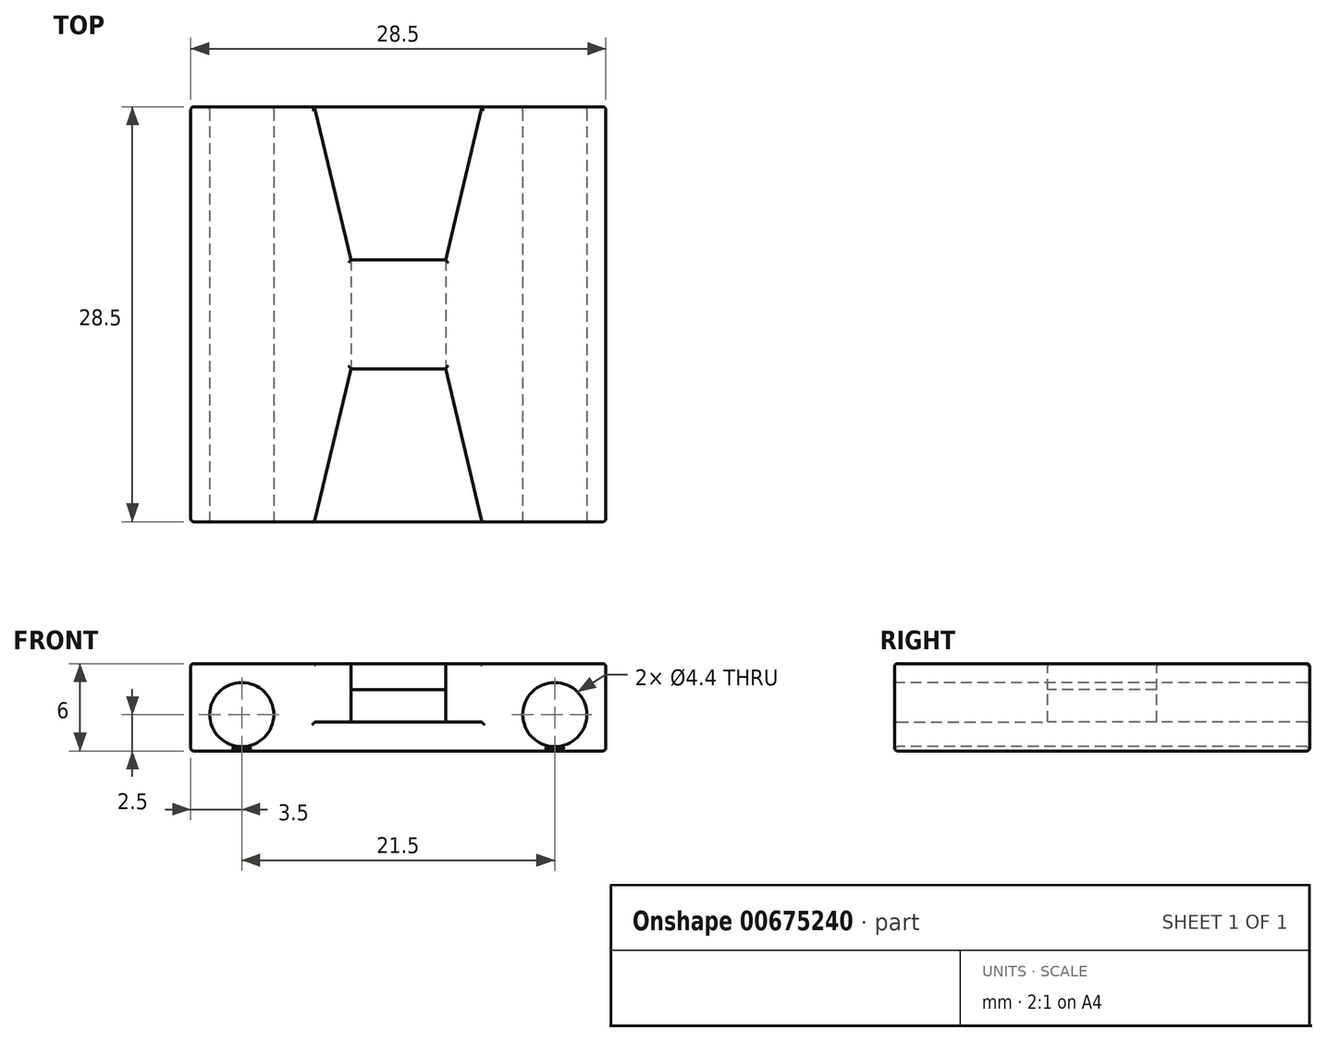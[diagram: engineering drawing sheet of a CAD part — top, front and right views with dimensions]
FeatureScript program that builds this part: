
annotation { "Feature Type Name" : "Feature", "Feature Type Description" : "" }
export const myFeature = defineFeature(function(context is Context, id is Id, definition is map)
    precondition{}
    {
        {
            var Q0;
            Q0=qCreatedBy(makeId("Top.planeOp"),FACE);
            var sketch = newSketch(context, id + "F0", { "sketchPlane" : qUnion([Q0])});
            skLineSegment(sketch, "E0.bottom", {"start": v(14.25, -14.25) * mm, "end": v(-14.25, -14.25) * mm});
            skLineSegment(sketch, "E0.top", {"start": v(14.25, 14.25) * mm, "end": v(-14.25, 14.25) * mm});
            skLineSegment(sketch, "E0.left", {"start": v(14.25, -14.25) * mm, "end": v(14.25, 14.25) * mm});
            skLineSegment(sketch, "E0.right", {"start": v(-14.25, -14.25) * mm, "end": v(-14.25, 14.25) * mm});
            skPoint(sketch, "E0.middle", {"position": v(0, 0) * mm});
            skSolve(sketch);
        }
        {
            var Q0;
            Q0 = qSketchRegion(id + "F0", true);
            extrude(context, id + "F1", {"entities" : qUnion([Q0]), "depth" : 6 * mm, "offsetDistance" : 25 * mm});
        }
        {
            var Q0;
            Q0=makeQuery(id+"F1.opExtrude","CAP_FACE",FACE,{"disambiguationData":[OSD([sQuery(id+"F0.wireOp",EDGE,"E0.bottom"),sQuery(id+"F0.wireOp",EDGE,"E0.top"),sQuery(id+"F0.wireOp",EDGE,"E0.left"),sQuery(id+"F0.wireOp",EDGE,"E0.right")])],"isStart":false});
            var sketch = newSketch(context, id + "F2", { "sketchPlane" : qUnion([Q0])});
            skLineSegment(sketch, "E1.bottom", {"start": v(3.25, 3.75) * mm, "end": v(-3.25, 3.75) * mm});
            skLineSegment(sketch, "E1.top", {"start": v(3.25, 14.25) * mm, "end": v(-3.25, 14.25) * mm});
            skLineSegment(sketch, "E1.left", {"start": v(3.25, 3.75) * mm, "end": v(3.25, 14.25) * mm});
            skLineSegment(sketch, "E1.right", {"start": v(-3.25, 3.75) * mm, "end": v(-3.25, 14.25) * mm});
            skPoint(sketch, "E1.middle", {"position": v(0, 9) * mm});
            skLineSegment(sketch, "E2", {"start": v(3.25, 14.25) * mm, "end": v(5.75, 14.25) * mm});
            skLineSegment(sketch, "E3", {"start": v(5.75, 14.25) * mm, "end": v(3.25, 3.75) * mm});
            skLineSegment(sketch, "E4", {"start": v(-3.25, 14.25) * mm, "end": v(-5.75, 14.25) * mm});
            skLineSegment(sketch, "E5", {"start": v(-5.75, 14.25) * mm, "end": v(-3.25, 3.75) * mm});
            skLineSegment(sketch, "E6.MirrorCS", {"start": v(-3.25, -14.25) * mm, "end": v(-5.75, -14.25) * mm});
            skLineSegment(sketch, "E7.MirrorCS", {"start": v(5.75, -14.25) * mm, "end": v(3.25, -3.75) * mm});
            skLineSegment(sketch, "E8.MirrorCS", {"start": v(-5.75, -14.25) * mm, "end": v(-3.25, -3.75) * mm});
            skLineSegment(sketch, "E9.MirrorCS", {"start": v(3.25, -14.25) * mm, "end": v(5.75, -14.25) * mm});
            skLineSegment(sketch, "E10.MirrorCS", {"start": v(-3.25, -3.75) * mm, "end": v(-3.25, -14.25) * mm});
            skLineSegment(sketch, "E11.MirrorCS", {"start": v(3.25, -3.75) * mm, "end": v(3.25, -14.25) * mm});
            skLineSegment(sketch, "E12.MirrorCS", {"start": v(3.25, -14.25) * mm, "end": v(-3.25, -14.25) * mm});
            skLineSegment(sketch, "E13.MirrorCS", {"start": v(3.25, -3.75) * mm, "end": v(-3.25, -3.75) * mm});
            skPoint(sketch, "E14.MirrorP", {"position": v(0, -9) * mm});
            skSolve(sketch);
        }
        {
            var Q0;
            Q0 = qSketchRegion(id + "F2", true);
            extrude(context, id + "F3", {"entities" : qUnion([Q0]), "operationType" : NewBodyOperationType.REMOVE, "oppositeDirection" : true, "depth" : 4 * mm, "offsetDistance" : 25 * mm});
        }
        {
            var Q0;
            Q0=makeQuery(id+"F1.opExtrude","SWEPT_FACE",FACE,{"disambiguationData":[OSD([sQuery(id+"F0.wireOp",EDGE,"E0.bottom")])]});
            var sketch = newSketch(context, id + "F4", { "sketchPlane" : qUnion([Q0])});
            skCircle(sketch, "E15", {"center": v(-10.75, 2.5) * mm, "radius": 2.2 * mm});
            skCircle(sketch, "E16.MirrorC", {"center": v(10.75, 2.5) * mm, "radius": 2.2 * mm});
            skSolve(sketch);
        }
        {
            var Q0;
            Q0 = qSketchRegion(id + "F4", true);
            extrude(context, id + "F5", {"entities" : qUnion([Q0]), "operationType" : NewBodyOperationType.REMOVE, "endBound" : BoundingType.THROUGH_ALL, "oppositeDirection" : true, "depth" : 25 * mm, "offsetDistance" : 25 * mm});
        }
        {
            var Q0;
            Q0=makeQuery(id+"F3.boolean.opBoolean","COPY",FACE,{"derivedFrom":makeQuery(id+"F3.opExtrude","SWEPT_FACE",FACE,{"disambiguationData":[OSD([sQuery(id+"F2.wireOp",EDGE,"E13.MirrorCS")])]})});
            var sketch = newSketch(context, id + "F6", { "sketchPlane" : qUnion([Q0])});
            skLineSegment(sketch, "E17.bottom", {"start": v(3.25, 2) * mm, "end": v(-3.25, 2) * mm});
            skLineSegment(sketch, "E17.top", {"start": v(3.25, 4.2) * mm, "end": v(-3.25, 4.2) * mm});
            skLineSegment(sketch, "E17.left", {"start": v(3.25, 2) * mm, "end": v(3.25, 4.2) * mm});
            skLineSegment(sketch, "E17.right", {"start": v(-3.25, 2) * mm, "end": v(-3.25, 4.2) * mm});
            skPoint(sketch, "E17.middle", {"position": v(0, 3.1) * mm});
            skSolve(sketch);
        }
        {
            var Q0;
            Q0 = qSketchRegion(id + "F6", true);
            extrude(context, id + "F7", {"entities" : qUnion([Q0]), "operationType" : NewBodyOperationType.REMOVE, "endBound" : BoundingType.THROUGH_ALL, "oppositeDirection" : true, "depth" : 25 * mm, "offsetDistance" : 25 * mm});
        }
        {
            var Q0;
            Q0=makeQuery(id+"F1.opExtrude","CAP_FACE",FACE,{"disambiguationData":[OSD([sQuery(id+"F0.wireOp",EDGE,"E0.bottom"),sQuery(id+"F0.wireOp",EDGE,"E0.top"),sQuery(id+"F0.wireOp",EDGE,"E0.left"),sQuery(id+"F0.wireOp",EDGE,"E0.right")])],"isStart":false});
            var Q1;
            Q1=makeQuery(id+"F1.opExtrude","SWEPT_FACE",FACE,{"disambiguationData":[OSD([sQuery(id+"F0.wireOp",EDGE,"E0.bottom")])]});
            var Q2;
            Q2=makeQuery(id+"F1.opExtrude","SWEPT_FACE",FACE,{"disambiguationData":[OSD([sQuery(id+"F0.wireOp",EDGE,"E0.top")])]});
            var Q3;
            Q3=makeQuery(id+"F1.opExtrude","CAP_FACE",FACE,{"disambiguationData":[OSD([sQuery(id+"F0.wireOp",EDGE,"E0.bottom"),sQuery(id+"F0.wireOp",EDGE,"E0.top"),sQuery(id+"F0.wireOp",EDGE,"E0.left"),sQuery(id+"F0.wireOp",EDGE,"E0.right")])],"isStart":true});
            fillet(context, id + "F8", {"entities" : qUnion([Q0, Q1, Q2, Q3]), "radius" : 0.2 * mm, "tangentPropagation" : true, "allowEdgeOverflow" : false});
        }
    });
